# Revit family: QF_BPRO_RWR-VP 163 KS_573388
name_source: partatom
category: Sonderausstattung
revit_build: Autodesk Revit 2018 (Build: 20190510_1515(x64)
units: mm (PartAtom-declared; Revit-internal decimal feet)

## family parameters
Arbeitsebenenbasiert = Nein
Beim Laden mit Abzugskörper schneiden = Nein
Bemaßung runder Anschluss = Durchmesser verwenden
Gemeinsam genutzt = Nein
Immer vertikal = Ja
Raumberechnungspunkt = Ja
Teiletyp = Normal

## types (1)
- RWR-VP 163 KS
    Abstand Einlagen = 117 mm  [stored 0.383858 ft]
    Anzahl Schienen = 12
    Artikel Nummer = 573388
    Beschreibung = Regalwagen aus rostfreiem Edelstahl
Auflagenabstand: 12 Paar 115 mm
Kapazität: 24 GN 1/1- oder EN-Tabletts
Tragfähigkeit: 200 kg
Stoßecken aus Kunststoff (Polyamid) an allen vier Ecken
    Beschreibung durch Hersteller analog Leistungsverzeichniskurztext = Abmessungen

Länge: 671 mm
Breite: 832 mm
Höhe: 1.675 mm
Abstand der Auflagenschienen: 115 mm

Ausführung

Der Regalwagen besteht aus CNS 18/10, Werkstoff-Nr. 1.4301. 
Zwischen stabilem Vierkantrohr mit 25 x 25 mm befinden sich
eingeschweißte U-Profil-Führungsschienen. Diese sind mit einer
Kippsicherung sowie einer beidseitigen Durchschubsicherung
versehen.
Der Regalwagen verfügt über einen Quereinschub für EN-Tabletts, 
dabei können 2 Tabletts hintereinander eingeschoben werden.
Ein eingeschweißtes Vierkantrohr 20 x 10 mm auf mittlerer Höhe
des Regalwagens, jeweils an Vorder- und Rückseite höhenversetzt
angebracht, erhöht zusätzlich die Stabilität.

Zur Vermeidung von Kälteverlusten ist der Regalwagen mit einer
durchgehenden Bodenplatte aus Edelstahl versehen.

Der Regalwagen ist fahrbar mittels rostfreien Kunststoffrollen
gemäß DIN 18867, Teil 8
(4 Lenkrollen, davon 2 mit Feststeller, Rollendurchmesser 125 mm).
Massive Stoßecken aus Kunststoff (Polyamid) an allen vier Ecken
schützen vor Beschädigung.

Zubehör/ Optionen

•	Staubschutzhaube aus durchsichtigem PE (Best.Nr. 573 018)
•	Isolierhaube aus PE, beidseitig aluminiert (Best.Nr. 573 017)
•	Transportsicherungsbügel, beidseitig

Technische Daten

Werkstoff:		Chromnickelstahl 18/10,
		Polyamid (PA)
Materialstärke VK-Rohr:	1,5 mm
Materialstärke
Auflageschienen:		1,2 mm
Gewicht:	20 kg
Tragfähigkeit je Wagen:	240 kg
Anzahl Auflagenpaare:	12
Kapazität:	24 EN-Tabletts

Besonderheit

•	U-Profil-Führungsschienen mit Kipp- und beidseitiger
Durchschubsicherung

Fabrikat

Hersteller:	B.PRO
Typ:                                       RWR-VP 163 KS
Best. Nr.:	573388
    Beschreibung durch Hersteller analog Leistungsverzeichnislangtext = Abmessungen

Länge: 671 mm
Breite: 832 mm
Höhe: 1.675 mm
Abstand der Auflagenschienen: 115 mm

Ausführung

Der Regalwagen besteht aus CNS 18/10, Werkstoff-Nr. 1.4301. 
Zwischen stabilem Vierkantrohr mit 25 x 25 mm befinden sich
eingeschweißte U-Profil-Führungsschienen. Diese sind mit einer
Kippsicherung sowie einer beidseitigen Durchschubsicherung
versehen.
Der Regalwagen verfügt über einen Quereinschub für EN-Tabletts, 
dabei können 2 Tabletts hintereinander eingeschoben werden.
Ein eingeschweißtes Vierkantrohr 20 x 10 mm auf mittlerer Höhe
des Regalwagens, jeweils an Vorder- und Rückseite höhenversetzt
angebracht, erhöht zusätzlich die Stabilität.

Zur Vermeidung von Kälteverlusten ist der Regalwagen mit einer
durchgehenden Bodenplatte aus Edelstahl versehen.

Der Regalwagen ist fahrbar mittels rostfreien Kunststoffrollen
gemäß DIN 18867, Teil 8
(4 Lenkrollen, davon 2 mit Feststeller, Rollendurchmesser 125 mm).
Massive Stoßecken aus Kunststoff (Polyamid) an allen vier Ecken
schützen vor Beschädigung.

Zubehör/ Optionen

•	Staubschutzhaube aus durchsichtigem PE (Best.Nr. 573 018)
•	Isolierhaube aus PE, beidseitig aluminiert (Best.Nr. 573 017)
•	Transportsicherungsbügel, beidseitig

Technische Daten

Werkstoff:		Chromnickelstahl 18/10,
		Polyamid (PA)
Materialstärke VK-Rohr:	1,5 mm
Materialstärke
Auflageschienen:		1,2 mm
Gewicht:	20 kg
Tragfähigkeit je Wagen:	240 kg
Anzahl Auflagenpaare:	12
Kapazität:	24 EN-Tabletts

Besonderheit

•	U-Profil-Führungsschienen mit Kipp- und beidseitiger
Durchschubsicherung

Fabrikat

Hersteller:	B.PRO
Typ:                                       RWR-VP 163 KS
Best. Nr.:	573388
    Gerätegewicht Netto = 20.00 kg
    Großküchengerätezuordnung = Ja
    Hersteller = B.PRO GmbH
    Höhe = 1675 mm  [stored 5.49541 ft]
    Internetadresse Gerätehersteller = https://www.bpro-solutions.com
    Internetadresse für Ersatzteilliste = https://www.bpro-solutions.com
    Kosten = 0 $
    Länge Gerätebreite = 671 mm
    Länge Korpus = 591 mm  [stored 1.93898 ft]
    Material = QF_Metal-Stainless-Steel_general
    Material_Stoßschutz = QF_Rubber-Black-Matt
    Modell = RWR 161
    Sockelhöhe = 160 mm  [stored 0.524934 ft]
    Tiefe = 832 mm
    Tiefe Korpus = 752 mm
    Typenkommentare = Regalwagen RWR-VP 163 KS
    URL = https://www.bpro-solutions.com
    Versatz Einlage unten = 69 mm

note: [stored X ft] marks values corroborated as IEEE doubles in the binary element streams (Revit-internal decimal feet)
